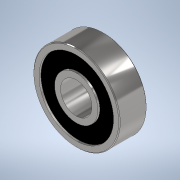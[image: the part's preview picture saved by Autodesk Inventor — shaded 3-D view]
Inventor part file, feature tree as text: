
AUTODESK INVENTOR PART (.ipt)
format: ipt  version: 2022 (Build 260153000, 153)  size: 158,208 bytes
history: native  units: mm
features: extrude x2, sketch x2, plane x1, mirror x1, chamfer x1, projected_geometry x1
ambient origin geometry x8: Origin, YZ Plane, XZ Plane, XY Plane, X Axis, Y Axis, Z Axis, Center Point
bodies: Solid1 (feature_tree)
feature tree (8):
  extrude  "Extrusion1"  Depth=22.0mm
  extrude  "Extrusion2"  Depth=0.5mm
  plane  "Work Plane1"
  mirror  "Mirror1"
  chamfer  "Chamfer1"  Distance=1.5mm
  sketch  "Sketch1"  dims[d0=8.0mm d1=22.0mm]
  sketch  "Sketch2"  dims[d2=7.0mm d3=0.0mm d4=1.5mm d5=1.5mm d6=0.5mm d7=0.0mm d8=0.2mm d9=2.0mm d10=45.0deg]
  projected_geometry  "Projected Loop1"
